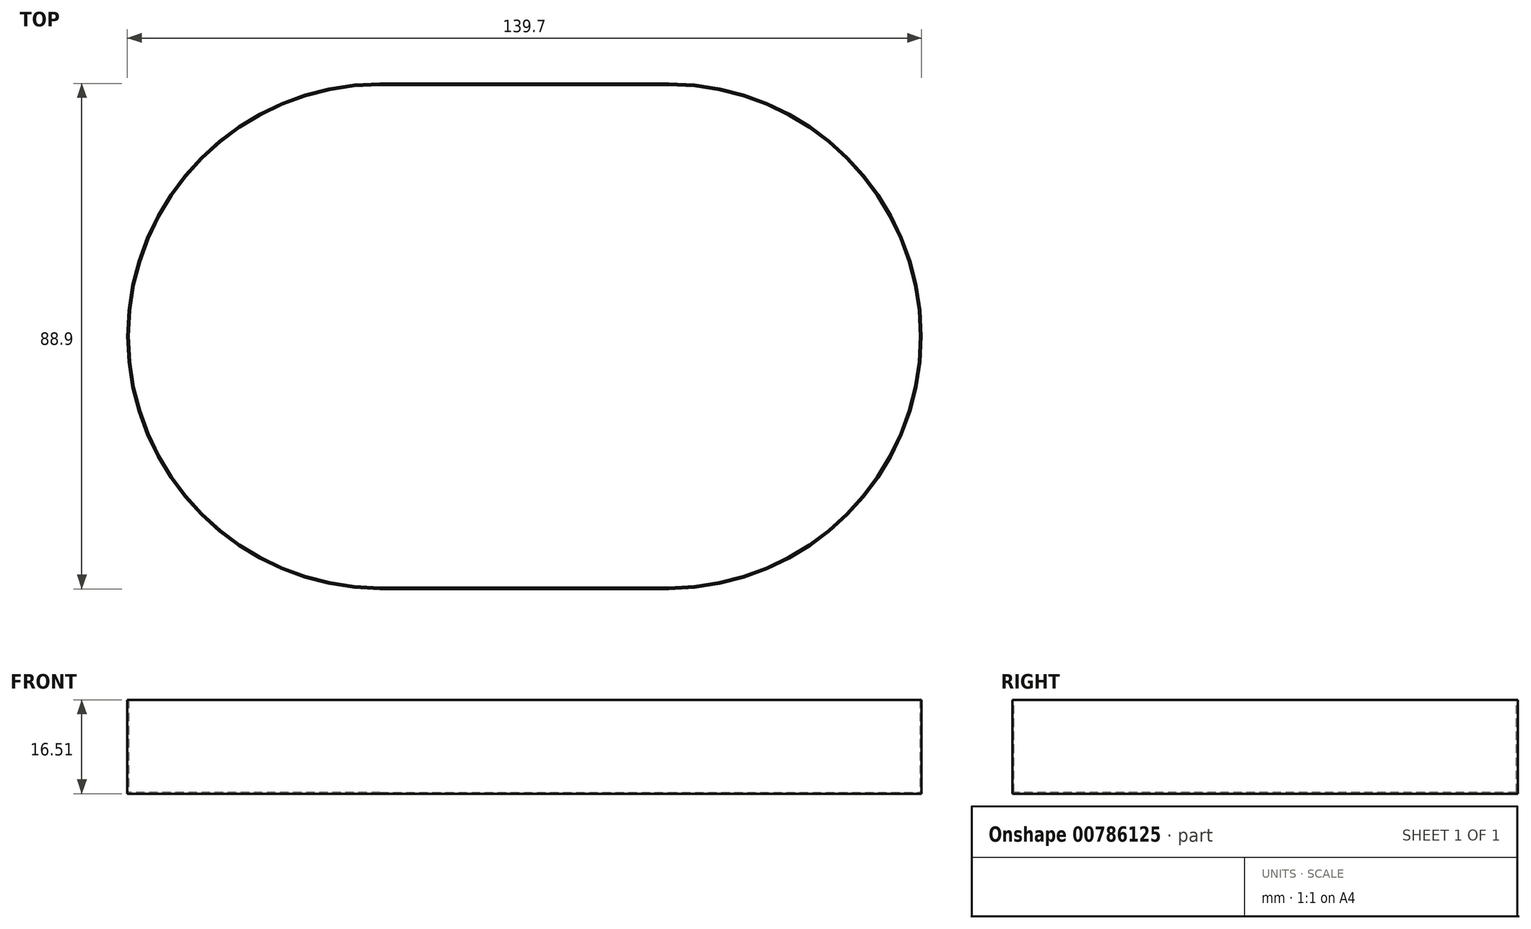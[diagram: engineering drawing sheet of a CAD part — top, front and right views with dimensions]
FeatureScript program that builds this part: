
annotation { "Feature Type Name" : "Feature", "Feature Type Description" : "" }
export const myFeature = defineFeature(function(context is Context, id is Id, definition is map)
    precondition{}
    {
        {
            var Q0;
            Q0=qCreatedBy(makeId("Top.planeOp"),FACE);
            var sketch = newSketch(context, id + "F0", { "sketchPlane" : qUnion([Q0])});
            skLineSegment(sketch, "E0.bottom", {"start": v(44.45, 0) * mm, "end": v(95.25, 0) * mm});
            skLineSegment(sketch, "E0.top", {"start": v(44.45, -88.9) * mm, "end": v(95.25, -88.9) * mm});
            skLineSegment(sketch, "E0.left", {"start": v(0, -44.45) * mm, "end": v(0, -44.45) * mm});
            skLineSegment(sketch, "E0.right", {"start": v(139.7, -44.45) * mm, "end": v(139.7, -44.45) * mm});
            skPoint(sketch, "E1.visualSharp", {"position": v(0, 0) * mm});
            skArc(sketch, "E1.filletArc", {"start": v(44.45, 0) * mm, "mid": v(13.02, -13.02) * mm, "end": v(0, -44.45) * mm});
            skPoint(sketch, "E2.visualSharp", {"position": v(0, -88.9) * mm});
            skArc(sketch, "E2.filletArc", {"start": v(0, -44.45) * mm, "mid": v(13.02, -75.88) * mm, "end": v(44.45, -88.9) * mm});
            skPoint(sketch, "E3.visualSharp", {"position": v(139.7, 0) * mm});
            skArc(sketch, "E3.filletArc", {"start": v(139.7, -44.45) * mm, "mid": v(126.68, -13.02) * mm, "end": v(95.25, 0) * mm});
            skPoint(sketch, "E4.visualSharp", {"position": v(139.7, -88.9) * mm});
            skArc(sketch, "E4.filletArc", {"start": v(95.25, -88.9) * mm, "mid": v(126.68, -75.88) * mm, "end": v(139.7, -44.45) * mm});
            skSolve(sketch);
        }
        {
            var Q0;
            Q0 = qSketchRegion(id + "F0", true);
            extrude(context, id + "F1", {"entities" : qUnion([Q0]), "depth" : 16.5 * mm, "offsetDistance" : 25.4 * mm});
        }
        {
            var Q0;
            Q0=makeQuery(id+"F1.opExtrude","CAP_FACE",FACE,{"disambiguationData":[OSD([sQuery(id+"F0.wireOp",EDGE,"E0.bottom"),sQuery(id+"F0.wireOp",EDGE,"E0.top"),sQuery(id+"F0.wireOp",EDGE,"E1.filletArc"),sQuery(id+"F0.wireOp",EDGE,"E2.filletArc"),sQuery(id+"F0.wireOp",EDGE,"E3.filletArc"),sQuery(id+"F0.wireOp",EDGE,"E4.filletArc")])],"isStart":false});
            shell(context, id + "F2", {"entities" : qUnion([Q0]), "thickness" : 0.25 * mm});
        }
    });
